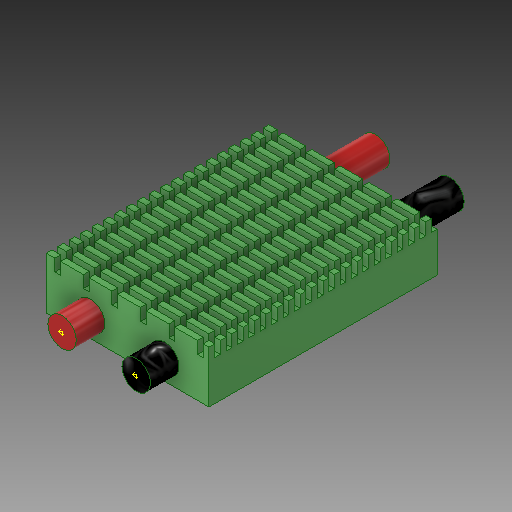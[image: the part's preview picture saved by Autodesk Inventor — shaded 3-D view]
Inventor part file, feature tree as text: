
AUTODESK INVENTOR PART (.ipt)
format: ipt  version: 2019.3 (Build 233278000, 278)  size: 914,432 bytes
history: native  units: mm
features: sketch x15, extrude x6, other x4, pattern_linear x2, emboss x2, projected_geometry x2, fillet x1
ambient origin geometry x8: Origin, YZ Plane, XZ Plane, XY Plane, X Axis, Y Axis, Z Axis, Center Point
bodies: Solid1 (feature_tree)
feature tree (32):
  extrude  "Extrusion1"  Depth=28.5mm
  sketch  "Sketch2"  dims[d2=9.1mm d3=0.0mm d4=1.0mm]
  extrude  "Extrusion2"  Depth=1.0mm
  pattern_linear  "Rectangular Pattern1"  Count1=6 Spacing1=5.0mm
  extrude  "Extrusion3"  Depth=2.0mm
  pattern_linear  "Rectangular Pattern2"  Spacing1=0.5mm  [1 undecoded]
  emboss  "Emboss1"
  extrude  "Extrusion4"  Depth=0.5mm
  extrude  "Extrusion5"  [1 undecoded]
  sketch  "Sketch7"  dims[d17=0.1mm d18=0.0mm]
  other  "OUT_NEGATIVE"
  sketch  "Sketch8"  dims[d19=5.0mm]
  other  "OUT_POSITIVE"
  sketch  "Sketch9"  dims[d20=6.5mm]
  other  "IN_POSITIVE"
  sketch  "Sketch10"  dims[d21=10.0mm d22=0.0mm]
  other  "IN_NEGATIVE"
  emboss  "Emboss2"
  extrude  "Extrusion6"  [1 undecoded]
  fillet  "Fillet1"  [1 undecoded]
  sketch  "Sketch13"  dims[d27=1.0mm]
  sketch  "Sketch14"  dims[d28=1.0mm]
  sketch  "Sketch15"  dims[d29=1.5mm d30=0.5mm d31=0.0mm d32=0.5mm]
  sketch  "Sketch1"  dims[d0=28.5mm d1=40.0mm]
  sketch  "Sketch3"  dims[d5=1.0mm]
  sketch  "Sketch4"  dims[d6=1.0mm]
  sketch  "Sketch5"  dims[d7=9.1mm d8=0.0mm d9=60.0mm d11=5.0mm]
  sketch  "Sketch6"  dims[d12=9.1mm d13=0.0mm d14=200.0mm d16=2.0mm]
  projected_geometry  "Projected Loop1"
  projected_geometry  "Projected Loop2"
  sketch  "Sketch11"  dims[d23=5.0mm d24=0.0mm]
  sketch  "Sketch12"  dims[d25=0.1mm d26=0.0mm]
note: 4 required parameter values undecoded (feature->parameter linkage not recoverable at this tier; creation-order binding heuristic only, values carry confidence <= 0.55)
